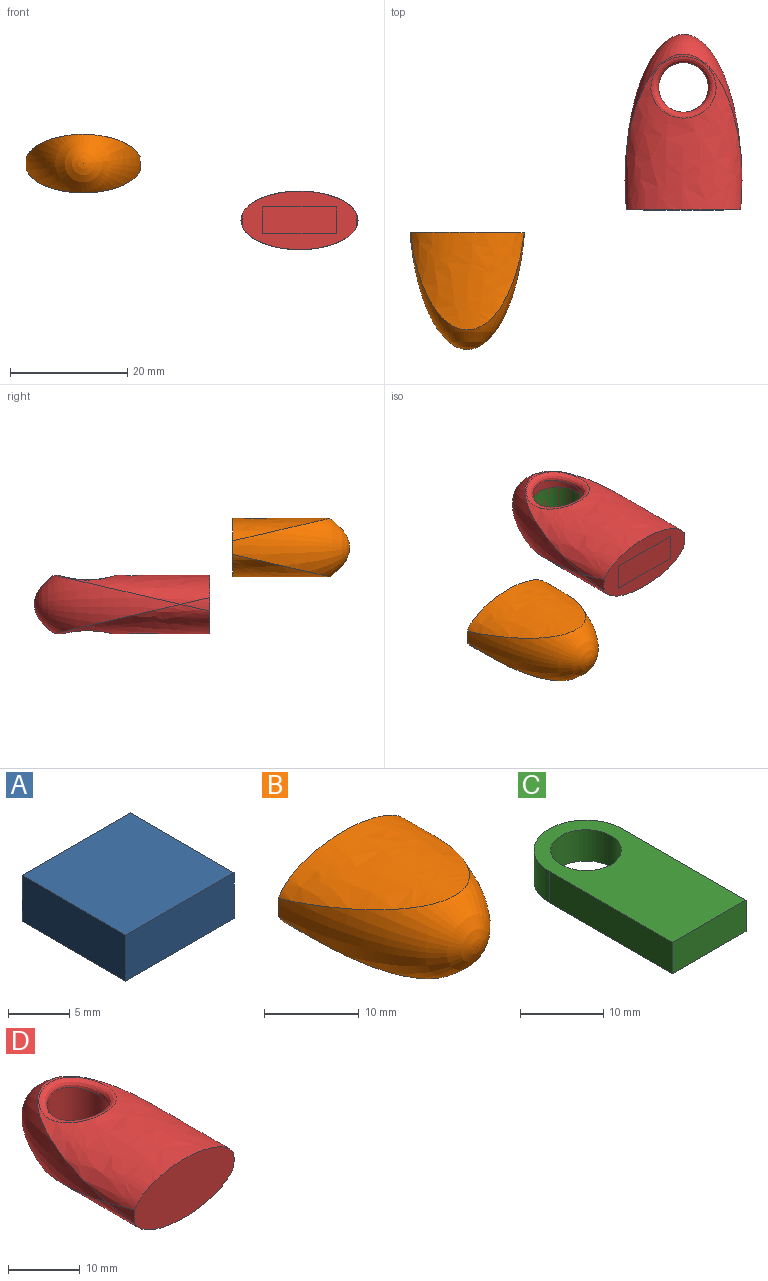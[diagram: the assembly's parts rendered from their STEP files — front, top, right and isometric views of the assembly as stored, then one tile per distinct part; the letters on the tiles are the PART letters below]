
ASSEMBLY  parts=4 mates=2
PART A: 6 faces, bbox 12.5x12x4.6 mm
  f0: plane 12.5x4.6mm, normal (0,-1,0), area 57.5mm2, adj f1,f2,f3,f4
  f1: plane 12.5x12mm, normal (0,0,1), area 150mm2, adj f0,f3,f4,f5
  f2: plane 12.5x12mm, normal (0,0,-1), area 150mm2, adj f0,f3,f4,f5
  f3: plane 12x4.6mm, normal (1,0,0), area 55.2mm2, adj f0,f1,f2,f5
  f4: plane 12x4.6mm, normal (-1,0,0), area 55.2mm2, adj f0,f1,f2,f5
  f5: plane 12.5x4.6mm, normal (0,1,0), area 57.5mm2, adj f1,f2,f3,f4
PART B: 4 faces, bbox 19.6x20x19.5 mm
  f0: extruded ~19.46x16.65mm, area 254.8mm2, adj f2,f3
  f1: extruded ~19.46x16.65mm, area 254.8mm2, adj f2,f3
  f2: revolved ~20x19.53mm, area 343.8mm2, adj f0,f1,f3
  f3: plane 19.6x10mm, normal (0,1,0), area 156.5mm2, adj f0,f1,f2
PART C: 7 faces, bbox 12.5x27.2x4.6 mm
  f0: plane 20.95x4.6mm, normal (-1,0,0), area 96.4mm2, adj f2,f3,f4,f6
  f1: plane 20.95x4.6mm, normal (1,0,0), area 96.4mm2, adj f2,f3,f4,f6
  f2: plane 27.2x12.5mm, normal (0,0,1), area 266.5mm2, adj f0,f1,f4,f5,f6
  f3: plane 27.2x12.5mm, normal (0,0,-1), area 266.5mm2, adj f0,f1,f4,f5,f6
  f4: cylinder r=6.25mm len=12.5mm, axis (0,0,-1), area 90.3mm2, adj f0,f1,f2,f3
  f5: cylinder r=4.25mm len=8.5mm, axis (0,0,-1), area 122.8mm2, adj f2,f3
  f6: plane 12.5x4.6mm, normal (0,-1,0), area 57.5mm2, adj f0,f1,f2,f3
PART D: 8 faces, bbox 20x30x20 mm
  f0: revolved ~5x2.36mm, area 5.8mm2, adj f2,f3,f6
  f1: revolved ~5x2.36mm, area 5.8mm2, adj f2,f3,f6
  f2: extruded ~26.66x20mm, area 428.2mm2, adj f0,f1,f4,f5,f6
  f3: extruded ~26.65x20mm, area 392.5mm2, adj f0,f1,f4,f6,f7
  f4: revolved ~25x20mm, area 355.4mm2, adj f2,f3
  f5: cylinder r=4.25mm len=9mm, axis (0,0,1), area 223.7mm2, adj f2,f7
  f6: plane 19.6x10mm, normal (0,-1,0), area 156.5mm2, adj f0,f1,f2,f3
  f7: bspline ~11.15x10.51mm, area 51mm2, adj f3,f5
PLACE A t=(17.94,17.5,-5.51)mm
PLACE B t=(17.94,1.55,-3.21)mm
PLACE C t=(54.89,21.37,-15.2)mm
PLACE D t=(54.89,5.42,-12.9)mm
MATE ball A.f5 <-> B.f3  axis (0,1,0) through (17.94,-3.45,-3.21)mm
MATE ball C.f6 <-> D.f6  axis (0,-1,0) through (54.89,0.42,-12.9)mm
